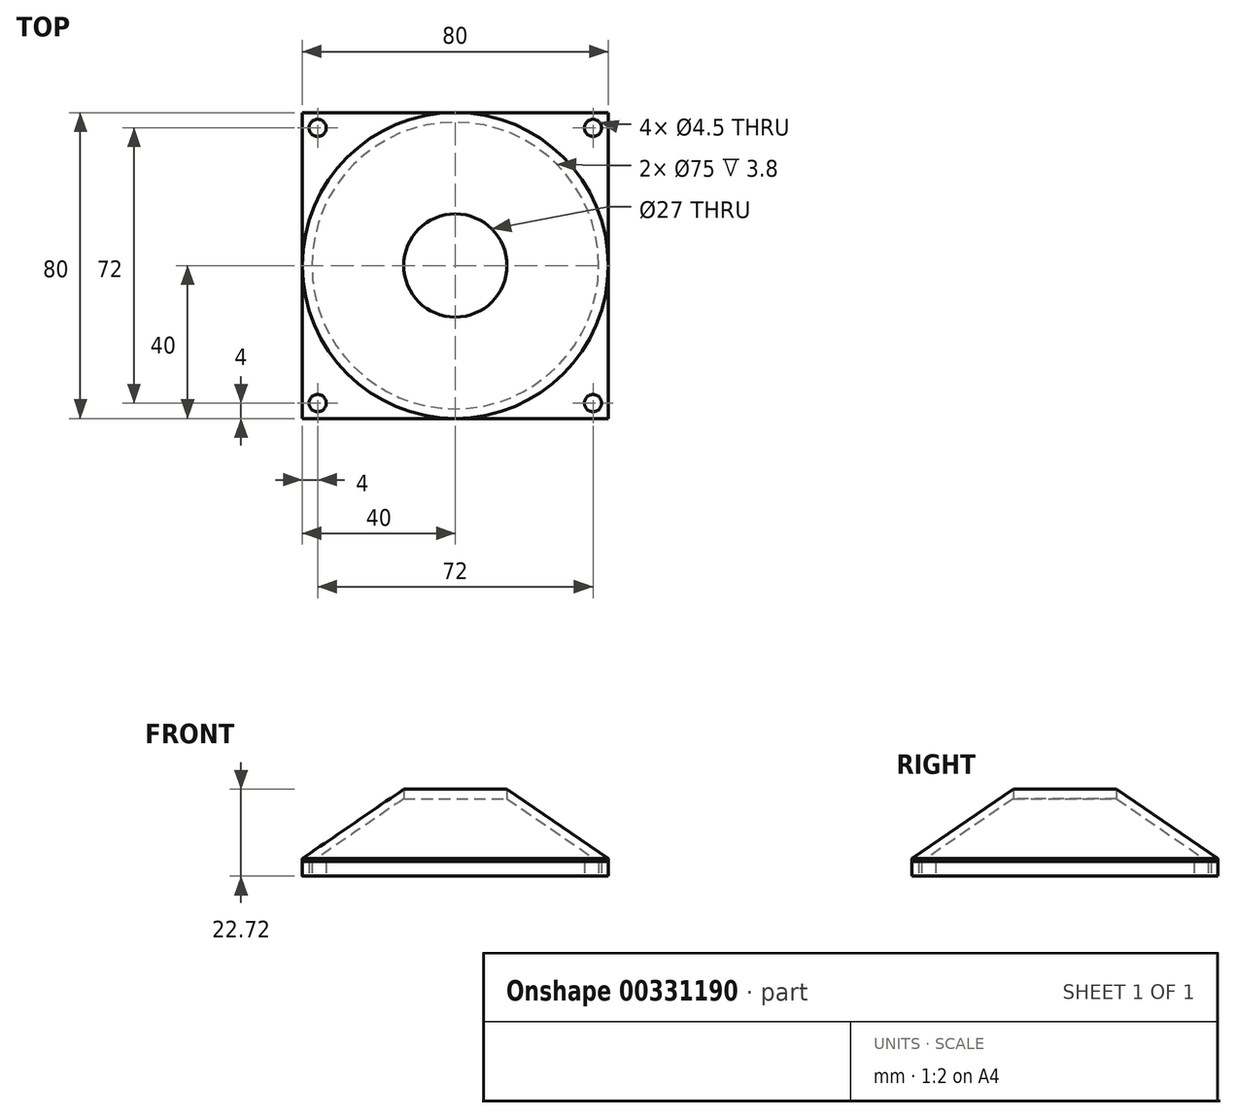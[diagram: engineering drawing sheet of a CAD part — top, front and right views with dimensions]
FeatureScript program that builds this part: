
annotation { "Feature Type Name" : "Feature", "Feature Type Description" : "" }
export const myFeature = defineFeature(function(context is Context, id is Id, definition is map)
    precondition{}
    {
        {
            var Q0;
            Q0=qCreatedBy(makeId("Top.planeOp"),FACE);
            var sketch = newSketch(context, id + "F0", { "sketchPlane" : qUnion([Q0])});
            skPoint(sketch, "E0.middle", {"position": v(0, 0) * mm});
            skCircle(sketch, "E1", {"center": v(0, 0) * mm, "radius": 37.5 * mm});
            skCircle(sketch, "E2", {"center": v(36, 36) * mm, "radius": 2.25 * mm});
            skPoint(sketch, "E3", {"position": v(37.62, 37.57) * mm});
            skCircle(sketch, "E4", {"center": v(36, -36) * mm, "radius": 2.25 * mm});
            skCircle(sketch, "E5", {"center": v(-36, -36) * mm, "radius": 2.25 * mm});
            skCircle(sketch, "E6", {"center": v(-36, 36) * mm, "radius": 2.25 * mm});
            skLineSegment(sketch, "E7.bottom", {"start": v(40, 40) * mm, "end": v(-40, 40) * mm});
            skLineSegment(sketch, "E7.top", {"start": v(40, -40) * mm, "end": v(-40, -40) * mm});
            skLineSegment(sketch, "E7.left", {"start": v(40, 40) * mm, "end": v(40, -40) * mm});
            skLineSegment(sketch, "E7.right", {"start": v(-40, 40) * mm, "end": v(-40, -40) * mm});
            skSolve(sketch);
        }
        {
            var Q0;
            Q0=makeQuery(id+"F0.imprint","IMPRINT",FACE,{"disambiguationData":[TD([[makeQuery(id+"F0.imprint","IMPRINT",EDGE,{"derivedFrom":sQuery(id+"F0.wireOp",EDGE,"E0.bottom")}),1.0]])]});
            var Q1;
            Q1=makeQuery(id+"F0.imprint","IMPRINT",FACE,{"disambiguationData":[TD([[makeQuery(id+"F0.imprint","IMPRINT",EDGE,{"derivedFrom":sQuery(id+"F0.wireOp",EDGE,"E1")}),-1.0]])]});
            extrude(context, id + "F1", {"entities" : qUnion([Q0, Q1]), "depth" : 3.8 * mm});
        }
        {
            var Q0;
            Q0=qCreatedBy(makeId("Right.planeOp"),FACE);
            var sketch = newSketch(context, id + "F2", { "sketchPlane" : qUnion([Q0])});
            skLineSegment(sketch, "E8", {"start": v(-37.5, 0) * mm, "end": v(-40, 0) * mm});
            skLineSegment(sketch, "E9", {"start": v(0, 0) * mm, "end": v(0, 55.75) * mm});
            skLineSegment(sketch, "E10", {"start": v(-40, 0) * mm, "end": v(-40, 3.8) * mm});
            skLineSegment(sketch, "E11", {"start": v(-37.5, 0) * mm, "end": v(-37.5, 3.8) * mm});
            skLineSegment(sketch, "E12", {"start": v(-13.5, 22.72) * mm, "end": v(-13.5, 20.22) * mm});
            skLineSegment(sketch, "E13", {"start": v(-13.5, 20.22) * mm, "end": v(-37.5, 3.8) * mm});
            skLineSegment(sketch, "E14", {"start": v(-13.5, 22.72) * mm, "end": v(-40, 4.59) * mm});
            skLineSegment(sketch, "E15", {"start": v(-40, 4.59) * mm, "end": v(-40, 3.8) * mm});
            skSolve(sketch);
        }
        {
            var Q0;
            Q0 = qSketchRegion(id + "F2", true);
            var Q1;
            Q1=sQuery(id+"F2.wireOp",EDGE,"E9");
            revolve(context, id + "F3", {"entities" : qUnion([Q0]), "axis" : qUnion([Q1]), "revolveType" : RevolveType.FULL});
        }
    });
